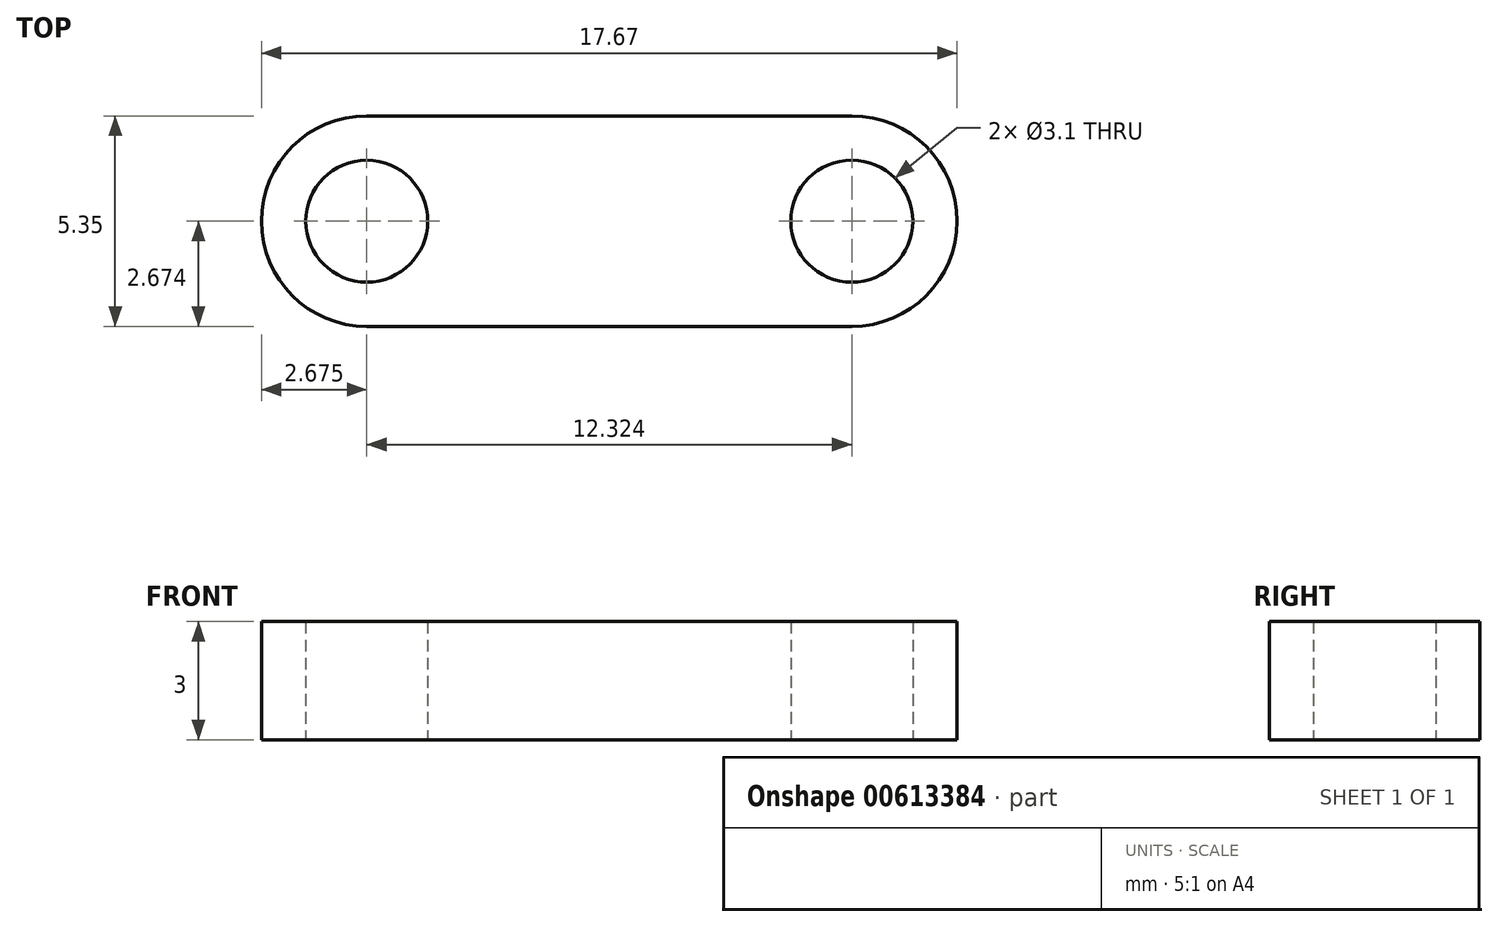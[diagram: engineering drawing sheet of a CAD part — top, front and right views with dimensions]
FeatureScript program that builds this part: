
annotation { "Feature Type Name" : "Feature", "Feature Type Description" : "" }
export const myFeature = defineFeature(function(context is Context, id is Id, definition is map)
    precondition{}
    {
        {
            var Q0;
            Q0=qCreatedBy(makeId("Top.planeOp"),FACE);
            var sketch = newSketch(context, id + "F0", { "sketchPlane" : qUnion([Q0])});
            skLineSegment(sketch, "E0.bottom", {"start": v(-45.4, 0) * mm, "end": v(-33.08, 0) * mm});
            skLineSegment(sketch, "E0.top", {"start": v(-45.4, -5.35) * mm, "end": v(-33.08, -5.35) * mm});
            skArc(sketch, "E1", {"start": v(-33.08, -5.35) * mm, "mid": v(-30.4, -2.68) * mm, "end": v(-33.08, 0) * mm});
            skArc(sketch, "E2", {"start": v(-45.4, 0) * mm, "mid": v(-48.08, -2.68) * mm, "end": v(-45.4, -5.35) * mm});
            skCircle(sketch, "E3", {"center": v(-45.4, -2.68) * mm, "radius": 1.55 * mm});
            skCircle(sketch, "E4", {"center": v(-33.08, -2.68) * mm, "radius": 1.55 * mm});
            skSolve(sketch);
        }
        {
            var Q0;
            Q0=makeQuery(id+"F0.imprint","IMPRINT",FACE,{"disambiguationData":[TD([[makeQuery(id+"F0.imprint","IMPRINT",EDGE,{"derivedFrom":sQuery(id+"F0.wireOp",EDGE,"E0.bottom")}),-1.0]])]});
            extrude(context, id + "F1", {"entities" : qUnion([Q0]), "depth" : 3 * mm, "offsetDistance" : 25 * mm});
        }
    });
